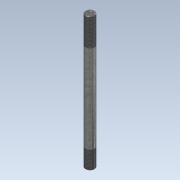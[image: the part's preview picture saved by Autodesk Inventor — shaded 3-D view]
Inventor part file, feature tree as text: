
AUTODESK INVENTOR PART (.ipt)
format: ipt  version: 2021 (Build 250183000, 183)  size: 138,240 bytes
history: native  units: mm
features: thread x2, extrude x1, plane x1, chamfer x1, sketch x1
ambient origin geometry x8: Origin, YZ Plane, XZ Plane, XY Plane, X Axis, Y Axis, Z Axis, Center Point
bodies: Solid1 (feature_tree)
feature tree (6):
  extrude  "Extrusion1"  Depth=145.4mm
  thread  "Thread1"  [1 undecoded]
  plane  "Work Plane1"
  thread  "Thread2"  [1 undecoded]
  chamfer  "Chamfer2"  Distance=30.0mm
  sketch  "Sketch1"  dims[d0=9.86mm d1=5.12mm d2=145.4mm d3=0.0mm d4=20.0mm d5=0.0mm d9=30.0mm d10=0.0mm d11=0.5mm d12=2.0mm d13=45.0deg]
note: 2 required parameter values undecoded (feature->parameter linkage not recoverable at this tier; creation-order binding heuristic only, values carry confidence <= 0.55)
